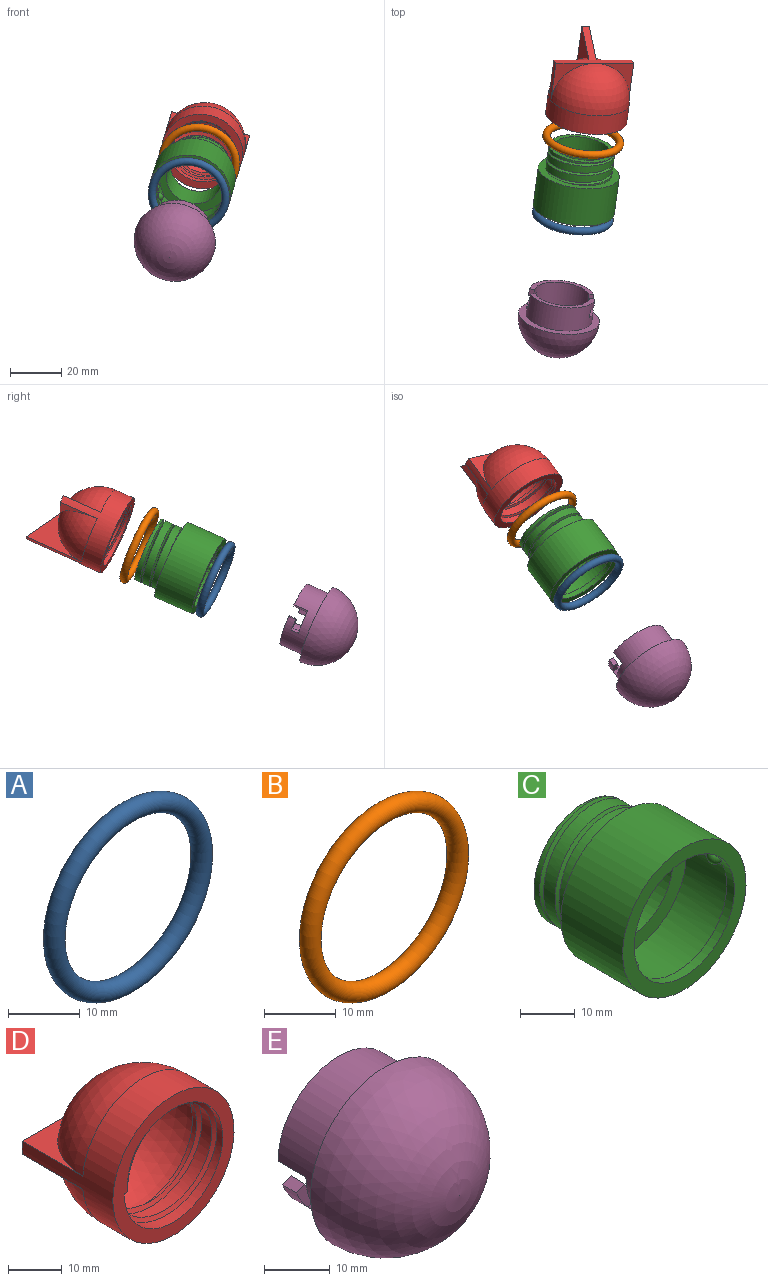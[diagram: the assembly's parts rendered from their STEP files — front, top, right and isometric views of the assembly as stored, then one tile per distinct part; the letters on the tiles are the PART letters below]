
ASSEMBLY  parts=5 mates=4
PART A: 1 faces, bbox 34.6x3x34.6 mm
  f0: torus R=14.5mm, axis (0,1,0), area 858.7mm2
PART B: 1 faces, bbox 34.6x3x34.6 mm
  f0: torus R=14.5mm, axis (0,1,0), area 858.7mm2
PART C: 24 faces, bbox 32.4x26.9x32.4 mm
  f0: cylinder r=13mm len=26mm, axis (0,-1,0), area 617.8mm2, adj f1,f6,f19,f20,f21,f23
  f1: plane 26.35x26.35mm, normal (0,1,0), area 145.8mm2, adj f0,f10,f19,f23
  f2: cylinder r=13mm len=26mm, axis (0,-1,0), area 230.4mm2, adj f3,f5,f8,f11,f12,f13,f14,f15
  f3: plane 25.08x19.97mm, normal (0,1,0), area 57.3mm2, adj f2,f4,f11,f15
  f4: cylinder r=14.5mm len=29mm, axis (0,1,0), area 1008.4mm2, adj f3,f8,f9,f11,f12,f13,f14,f15
  f5: plane 32x32mm, normal (0,-1,0), area 273.3mm2, adj f2,f7
  f6: plane 32x32mm, normal (0,1,0), area 273.3mm2, adj f0,f7,f22
  f7: cylinder r=16mm len=32mm, axis (0,1,0), area 1608.5mm2, adj f5,f6
  f8: plane 25.08x19.97mm, normal (0,1,0), area 57.3mm2, adj f2,f4,f12,f14
  f9: plane 29x29mm, normal (0,-1,0), area 280.4mm2, adj f4,f10
  f10: cylinder r=11mm len=22mm, axis (0,-1,0), area 829.4mm2, adj f1,f9
  f11: plane 8x1.39mm, normal (0.38,0,-0.93), area 12mm2, adj f2,f3,f4,f13
  f12: plane 8x1.09mm, normal (-0.68,0,0.73), area 12mm2, adj f2,f4,f8,f13
  f13: plane 5.01x3.94mm, normal (0,1,0), area 7.5mm2, adj f2,f4,f11,f12
  f14: plane 8x1.39mm, normal (-0.38,0,0.93), area 12mm2, adj f2,f4,f8,f16
  f15: plane 8x1.09mm, normal (0.68,0,-0.73), area 12mm2, adj f2,f3,f4,f16
  f16: plane 5.01x3.94mm, normal (0,1,0), area 7.5mm2, adj f2,f4,f14,f15
  f17: sphere r=1.5mm, area 13.7mm2, adj f2
  f18: sphere r=1.5mm, area 13.7mm2, adj f2
  f19: plane 1x0.5mm, normal (0,0,1), area 0.3mm2, adj f0,f1,f21
  f20: plane 1x1mm, normal (0,0,1), area 0.5mm2, adj f0,f21,f22,f23
  f21: bspline ~30.02x26mm, area 219.7mm2, adj f0,f19,f20,f22,f23
  f22: cylinder r=13mm len=9.11mm, axis (0,-1,0), area 2.5mm2, adj f6,f20,f21
  f23: bspline ~30.02x26mm, area 214.4mm2, adj f0,f1,f20,f21
PART D: 21 faces, bbox 32x32.5x32 mm
  f0: plane 0.9x0.45mm, normal (0,0,-1), area 0.2mm2, adj f7,f15,f18
  f1: bspline ~30.02x26mm, area 154.3mm2, adj f7,f15,f17,f18
  f2: plane 24x14.43mm, normal (1,0,0), area 113.2mm2, adj f3,f4,f6,f14
  f3: sphere r=16mm, area 329mm2, adj f2,f4,f6
  f4: plane 16x14.43mm, normal (0,0,-1), area 55.4mm2, adj f2,f3,f6,f10
  f5: sphere r=16mm, area 329mm2, adj f6,f9,f13
  f6: cylinder r=16mm len=32mm, axis (0,1,0), area 972.5mm2, adj f2,f3,f4,f5,f7,f8,f9,f10
  f7: plane 32x32mm, normal (0,-1,0), area 277.4mm2, adj f0,f1,f6,f15
  f8: sphere r=16mm, area 728.8mm2, adj f6,f11
  f9: plane 16x14.43mm, normal (0,0,-1), area 55.4mm2, adj f5,f6,f10,f13
  f10: plane 32x3mm, normal (0,1,0), area 95.9mm2, adj f4,f6,f9,f11,f14
  f11: plane 31.86x16mm, normal (0,0,1), area 111.2mm2, adj f6,f8,f10
  f12: plane 3x0.07mm, normal (0,1,0), area 0.1mm2, adj f6,f14
  f13: plane 24x14.43mm, normal (-1,0,0), area 113.2mm2, adj f5,f6,f9,f14
  f14: plane 14.43x8mm, normal (0,0.87,0.48), area 49.5mm2, adj f2,f10,f12,f13
  f15: cylinder r=13mm len=26mm, axis (0,-1,0), area 510.6mm2, adj f0,f1,f7,f17,f18,f19
  f16: cylinder r=13mm len=8.37mm, axis (0,1,0), area 2.1mm2, adj f17,f18,f19
  f17: plane 0.9x0.9mm, normal (0,0,1), area 0.4mm2, adj f1,f15,f16,f18
  f18: bspline ~30.02x26mm, area 158.9mm2, adj f0,f1,f15,f16,f17
  f19: plane 29x29mm, normal (0,1,0), area 129.6mm2, adj f15,f16,f20
  f20: sphere r=14.5mm, area 1321mm2, adj f19
PART E: 17 faces, bbox 32x26x32 mm
  f0: cylinder r=11mm len=22mm, axis (0,1,0), area 1268.9mm2, adj f2,f3,f6,f7,f8,f9,f10,f11
  f1: cylinder r=13mm len=26mm, axis (0,1,0), area 727.9mm2, adj f2,f3,f4,f7,f8,f9,f10,f11
  f2: plane 25.04x13mm, normal (0,1,0), area 66.1mm2, adj f0,f1,f7,f10
  f3: plane 25.04x13mm, normal (0,1,0), area 66.1mm2, adj f0,f1,f8,f11
  f4: plane 32x32mm, normal (0,1,0), area 273.3mm2, adj f1,f5
  f5: sphere r=16mm, area 1608.5mm2, adj f4
  f6: sphere r=14.5mm, area 460.3mm2, adj f0
  f7: plane 6x2mm, normal (0,0,-1), area 12mm2, adj f0,f1,f2,f9
  f8: plane 3x1.85mm, normal (-0.38,0,0.93), area 6mm2, adj f0,f1,f3,f15
  f9: plane 8.89x4.97mm, normal (0,1,0), area 18.1mm2, adj f0,f1,f7,f16
  f10: plane 3x1.85mm, normal (0.38,0,-0.93), area 6mm2, adj f0,f1,f2,f13
  f11: plane 6x2mm, normal (0,0,1), area 12mm2, adj f0,f1,f3,f12
  f12: plane 8.89x4.97mm, normal (0,1,0), area 18.1mm2, adj f0,f1,f11,f14
  f13: plane 4.74x4.01mm, normal (0,-1,0), area 8.8mm2, adj f0,f1,f10,f14
  f14: plane 3x1.46mm, normal (0.68,0,-0.73), area 6mm2, adj f0,f1,f12,f13
  f15: plane 4.74x4.01mm, normal (0,-1,0), area 8.8mm2, adj f0,f1,f8,f16
  f16: plane 3x1.46mm, normal (-0.68,0,0.73), area 6mm2, adj f0,f1,f9,f15
PLACE A rot(axis=(0.82,0.56,-0.12),30.2deg) t=(-13.84,-5.92,2.32)mm
PLACE B rot(axis=(0.82,0.56,-0.12),30.2deg) t=(-11.64,10.24,9.53)mm
PLACE C rot(axis=(0.82,0.56,-0.12),30.2deg) t=(-13.48,-3.27,3.51)mm
PLACE D rot(axis=(0.82,0.56,-0.12),30.2deg) t=(-10.58,18.04,13.01)mm
PLACE E rot(axis=(0.82,0.56,-0.12),30.2deg) t=(-19.27,-45.68,-15.4)mm
MATE slider A.f0 <-> E.f0  axis (0.12,0.91,0.4) through (-13.84,-5.92,2.32)mm
MATE slider E.f0 <-> C.f2  axis (0.12,0.91,0.4) through (-18.65,-41.15,-13.38)mm
MATE slider B.f0 <-> C.f0  axis (0.12,0.91,0.4) through (-9.77,23.92,15.63)mm
MATE slider D.f15 <-> C.f0  axis (-0.12,-0.91,-0.4) through (-8.1,36.16,21.09)mm
